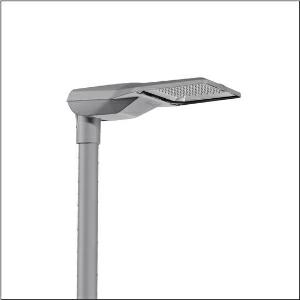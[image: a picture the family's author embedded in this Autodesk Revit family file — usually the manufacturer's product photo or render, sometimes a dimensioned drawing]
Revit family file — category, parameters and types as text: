
# Revit family: streetlight_sl_21_midi___stw1_0a_5xe7e33a08mb_c91c
name_source: partatom
category: Lighting Fixtures
units: mm (PartAtom-declared; Revit-internal decimal feet)

## family parameters
Cut with Voids When Loaded = No
Host = Face
Light Source = No
Part Type = Normal
Room Calculation Point = No
Round Connector Dimension = Use Diameter
Shared = No

## types (1)
- --- (1 x LED, 18270 lm, 136 W, 3000K)
    Apparent Load = 136 VA
    CIE Flux Codes = 38 75 98 100 100
    Color Rendering = 70
    Color Temperature = 3000K
    Default Elevation = 1800 mm
    Description = Streetlight SL 21 midi, mast luminaire, primary light control with lens, of PMMA, primary optical cover: cover, of toughened safety glass, transparent, light distribution: STW1.0a, light emission: direct distribution, primary light characteristic: asymmetric, installation type: post-top, side-entry, LED, 3G 1.5mm², High Power LED, rated luminous flux: 18.270lm, luminous efficacy: 134lm/W, light colour: 730, colour temperature: 3000K, control: overheat protection, constant luminous flux control, time-dependent luminous flux control, flexible luminous flux parameterisation, mains connection: 220..240V, AC, 50/60Hz, connection cable pre-assembled, cable length: 12,5m, wiring characteristics: H07RN-F, start of lifetime: 136W, end of service life: 142W, reduction: 61W, luminaire housing, of diecast aluminium, powder-coated, Siteco® metallic grey (DB 702S), corrosivity category C5 mid according to DIN EN ISO 12944, please order mast flange separately, inclination adjustable: 0°, 5°, 10°, 15°, sealing non-destructively replaceable, multi-level sealing system, length: 644mm, width: 335mm, height: 110mm, mast flange for spigot size: 42mm (side-entry): 5XC10008XM4, 60/48mm (side-entry/post-top): 5XC10108XM2, 76/60mm (side-entry/post-top): 5XC10108XM1, protection rating (complete): IP66, insulation class (complete): insulation class II (safety insulation), certification: CE, ENEC, ENEC+, VDE, impact resistance: IK09, permissible operating ambient temperature for outdoor applications: -40..+50°C, standard-compliant lighting for roads and squares, packaging unit: 1 piece

Light Distribution: STW1.0a
    Height = 111 mm
    Lamp = 1 x LED
    Lamp Light Flux = 18270 lm
    Lamp Power = 136 W
    Lamp count = 1
    Length = 644 mm
    Luminous efficacy = 134 lm/W
    Manufacturer = Siteco
    ModVariant = No
    Model = 5XE7E33A08MB
    Number of Poles = 1
    OnlyDefault = Yes
    Power Factor = 1
    Product Name = Streetlight SL 21 midi | STW1.0a
    Product group = mast luminaire | pylon top
    ProductGroupID = 6100
    Protection Class = Protection class II
    Protection Degree = IP 66
    RLX_Detail_Level = 1
    RLX_Emergency_Light_Flux = 0 lm
    RLX_Emergency_Type = 0
    RLX_Emergency_Type_DB = No
    RlxData = <blob elided: 90465 chars, md5=02048ec4>
    Socket = socket
    Standby Power = 0 W
    System Light Flux = 18270 lm
    System Power = 136 W
    Type Comments = factory setting: luminous flux: 100 % | Output Level: 100 % | 695 mA
    Type Image = l_1004298.jpg
    URL = http://relux.com
    VarID = @adj_139503
    Voltage = 0 V
    Weight = 0.00 kg
    Width = 336 mm

## geometry (parser evidence)
native form markers: Blend x4, Sweep x10
no freeform markers — native parametric forms only
